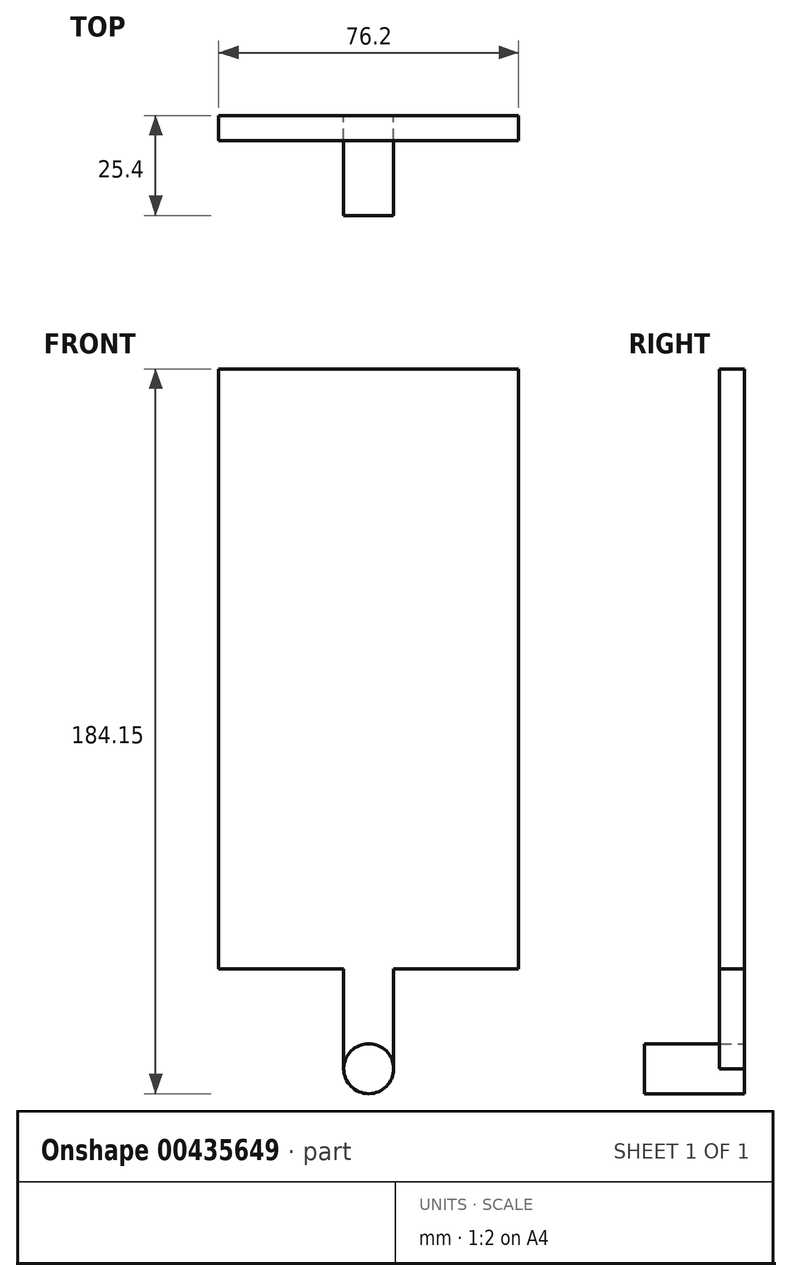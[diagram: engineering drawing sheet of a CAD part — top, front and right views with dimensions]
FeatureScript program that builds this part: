
annotation { "Feature Type Name" : "Feature", "Feature Type Description" : "" }
export const myFeature = defineFeature(function(context is Context, id is Id, definition is map)
    precondition{}
    {
        {
            var Q0;
            Q0=qCreatedBy(makeId("Front.planeOp"),FACE);
            var sketch = newSketch(context, id + "F0", { "sketchPlane" : qUnion([Q0])});
            skLineSegment(sketch, "E0.bottom", {"start": v(38.1, -76.2) * mm, "end": v(-38.1, -76.2) * mm});
            skLineSegment(sketch, "E0.top", {"start": v(38.1, 76.2) * mm, "end": v(-38.1, 76.2) * mm});
            skLineSegment(sketch, "E0.left", {"start": v(38.1, -76.2) * mm, "end": v(38.1, 76.2) * mm});
            skLineSegment(sketch, "E0.right", {"start": v(-38.1, -76.2) * mm, "end": v(-38.1, 76.2) * mm});
            skPoint(sketch, "E0.middle", {"position": v(0, 0) * mm});
            skCircle(sketch, "E1", {"center": v(0, -101.6) * mm, "radius": 6.35 * mm});
            skLineSegment(sketch, "E2", {"start": v(-6.35, -101.6) * mm, "end": v(-6.35, -76.2) * mm});
            skLineSegment(sketch, "E3.MirrorCS", {"start": v(6.35, -101.6) * mm, "end": v(6.35, -76.2) * mm});
            skSolve(sketch);
        }
        {
            var Q0;
            Q0=makeQuery(id+"F0.imprint","IMPRINT",FACE,{"disambiguationData":[TD([[makeQuery(id+"F0.imprint","IMPRINT",EDGE,{"derivedFrom":sQuery(id+"F0.wireOp",EDGE,"E0.top")}),1.0]])]});
            var Q1;
            {var subQ0=sQuery(id+"F0.wireOp",EDGE,"E2");Q1=makeQuery(id+"F0.imprint","IMPRINT",FACE,{"disambiguationData":[TD([[makeQuery(id+"F0.imprint","IMPRINT",EDGE,{"derivedFrom":subQ0}),-1.0]])]});}
            extrude(context, id + "F1", {"entities" : qUnion([Q0, Q1]), "depth" : 6.35 * mm});
        }
        {
            var Q0;
            {var subQ0=sQuery(id+"F0.wireOp",EDGE,"E1");var subQ1=makeQuery(id+"F0.imprint","INTERSECT",VERTEX,{"derivedFrom":[subQ0,sQuery(id+"F0.wireOp",EDGE,"E2")]});Q0=makeQuery(id+"F0.imprint","IMPRINT",FACE,{"disambiguationData":[TD([[makeQuery(id+"F0.imprint","IMPRINT",EDGE,{"disambiguationData":[TD([[subQ1,1.0]])],"derivedFrom":subQ0}),1.0]])]});}
            extrude(context, id + "F2", {"entities" : qUnion([Q0]), "depth" : 25.4 * mm});
        }
    });
